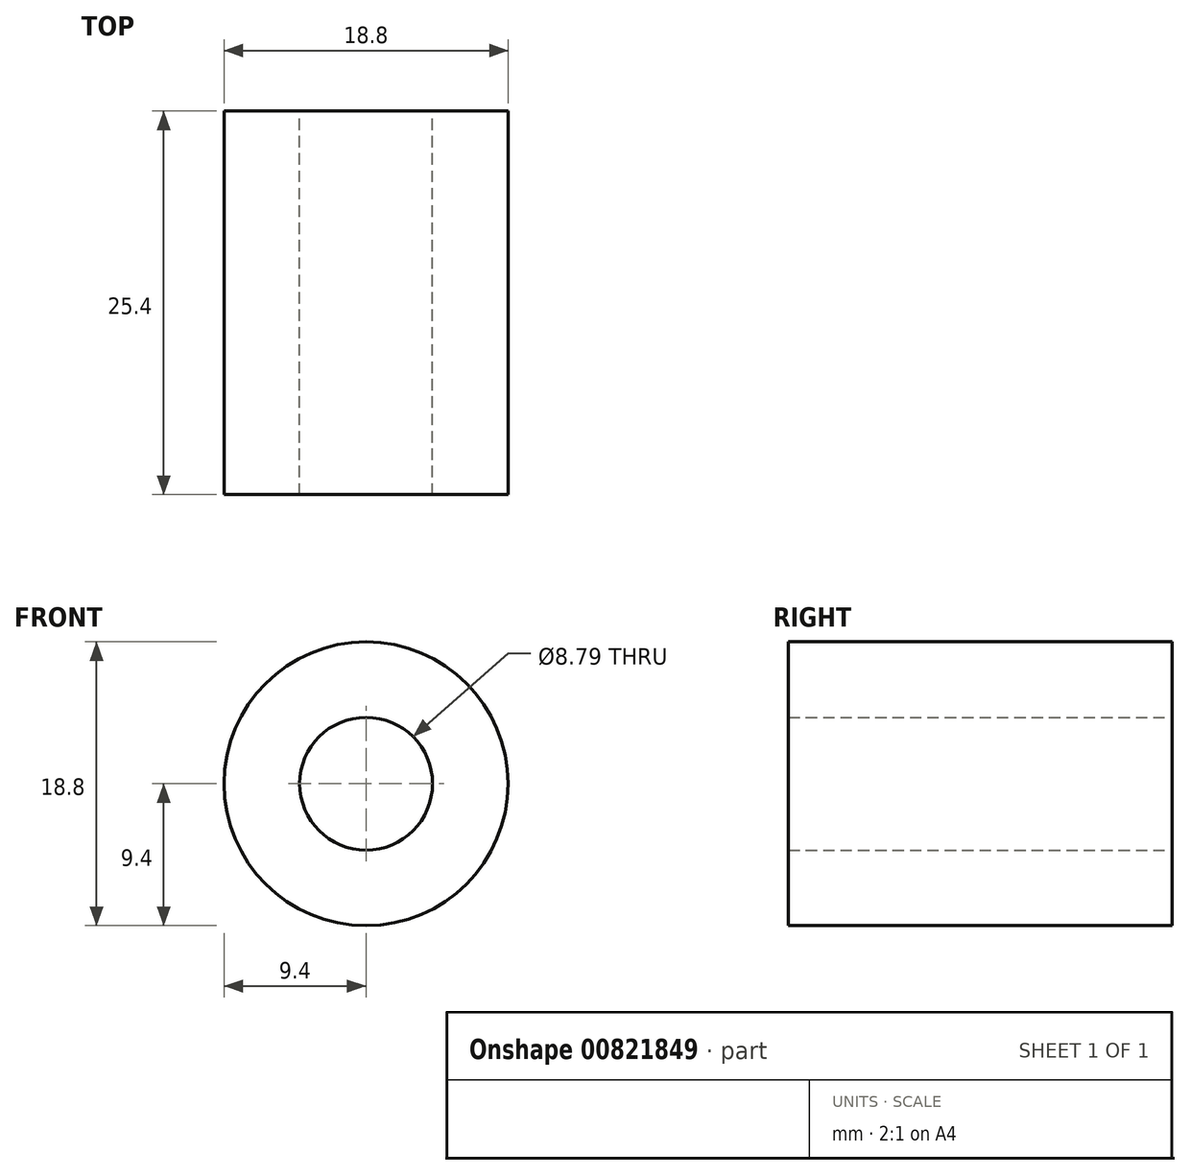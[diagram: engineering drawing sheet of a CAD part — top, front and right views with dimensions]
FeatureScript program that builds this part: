
annotation { "Feature Type Name" : "Feature", "Feature Type Description" : "" }
export const myFeature = defineFeature(function(context is Context, id is Id, definition is map)
    precondition{}
    {
        {
            var Q0;
            Q0=qCreatedBy(makeId("Front.planeOp"),FACE);
            var sketch = newSketch(context, id + "F0", { "sketchPlane" : qUnion([Q0])});
            skCircle(sketch, "E0", {"center": v(0, 0) * mm, "radius": 9.4 * mm});
            skCircle(sketch, "E1", {"center": v(0, 0) * mm, "radius": 4.4 * mm});
            skSolve(sketch);
        }
        {
            var Q0;
            Q0 = qSketchRegion(id + "F0", true);
            extrude(context, id + "F1", {"entities" : qUnion([Q0]), "depth" : 25.4 * mm, "offsetDistance" : 25.4 * mm});
        }
    });
